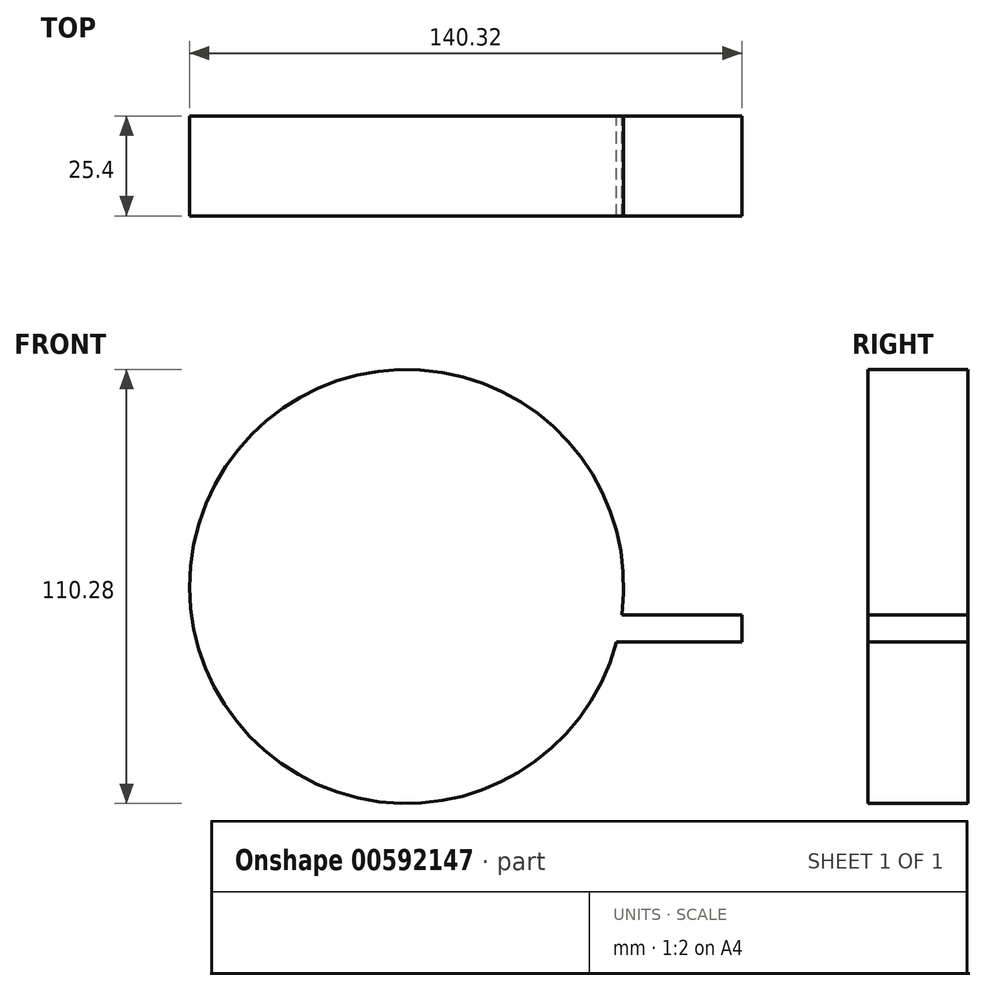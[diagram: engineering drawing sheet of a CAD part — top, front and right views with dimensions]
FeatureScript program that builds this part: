
annotation { "Feature Type Name" : "Feature", "Feature Type Description" : "" }
export const myFeature = defineFeature(function(context is Context, id is Id, definition is map)
    precondition{}
    {
        {
            var Q0;
            Q0=qCreatedBy(makeId("Front.planeOp"),FACE);
            var sketch = newSketch(context, id + "F0", { "sketchPlane" : qUnion([Q0])});
            skCircle(sketch, "E0", {"center": v(0, 0) * mm, "radius": 55.14 * mm});
            skLineSegment(sketch, "E1.bottom", {"start": v(0, 0) * mm, "end": v(117.23, 0) * mm});
            skLineSegment(sketch, "E1.top", {"start": v(51.22, -20.54) * mm, "end": v(117.23, -20.54) * mm});
            skLineSegment(sketch, "E1.right", {"start": v(117.23, 0) * mm, "end": v(117.23, -20.54) * mm});
            skLineSegment(sketch, "E2.bottom", {"start": v(54.67, -7.18) * mm, "end": v(85.18, -7.18) * mm});
            skLineSegment(sketch, "E2.top", {"start": v(53.3, -14.12) * mm, "end": v(85.18, -14.12) * mm});
            skLineSegment(sketch, "E2.right", {"start": v(85.18, -7.18) * mm, "end": v(85.18, -14.12) * mm});
            skSolve(sketch);
        }
        {
            var Q0;
            {var subQ0=sQuery(id+"F0.wireOp",EDGE,"E2.bottom");Q0=makeQuery(id+"F0.imprint","IMPRINT",FACE,{"disambiguationData":[TD([[makeQuery(id+"F0.imprint","IMPRINT",EDGE,{"derivedFrom":subQ0}),-1.0]])]});}
            var Q1;
            {var subQ0=sQuery(id+"F0.wireOp",EDGE,"E0");var subQ1=makeQuery(id+"F0.imprint","INTERSECT",VERTEX,{"derivedFrom":[subQ0,sQuery(id+"F0.wireOp",EDGE,"E2.bottom")]});Q1=makeQuery(id+"F0.imprint","IMPRINT",FACE,{"disambiguationData":[TD([[makeQuery(id+"F0.imprint","IMPRINT",EDGE,{"disambiguationData":[TD([[subQ1,-1.0]])],"derivedFrom":subQ0}),1.0]])]});}
            extrude(context, id + "F1", {"entities" : qUnion([Q0, Q1]), "depth" : 25.4 * mm, "offsetDistance" : 25.4 * mm});
        }
    });
